# Revit family: FU_Stool_Sandler_Fly 3-4
name_source: partatom
category: Furniture
units: mm (PartAtom-declared; Revit-internal decimal feet)

## family parameters
Always vertical = Yes
Cut with Voids When Loaded = No
OmniClass Number = 23.40.20.00
OmniClass Title = General Furniture and Specialties
Room Calculation Point = No
Shared = No
Work Plane-Based = No

## types (1)
- Fly 3.4
    Back = Fabric - Gravity - Frost CPC32
    Default Elevation = 0 mm  [stored 0 ft]
    Depth = 535 mm  [stored 1.75525 ft]
    Description = Barstool with an upholstered back, a solid beech seat and frame, fitted with a stainless steel kick-plate on the front footrest.
    Frame = Wood -  Aniline - White
    Height = 1080 mm  [stored 3.54331 ft]
    Manufacturer = Sandler
    Model = Fly 3.4
    URL = https://www.sandlerseating.com
    Width = 540 mm  [stored 1.77165 ft]

note: [stored X ft] marks values corroborated as IEEE doubles in the binary element streams (Revit-internal decimal feet)

## geometry (parser evidence)
native form markers: Sweep x4
no freeform markers — native parametric forms only
